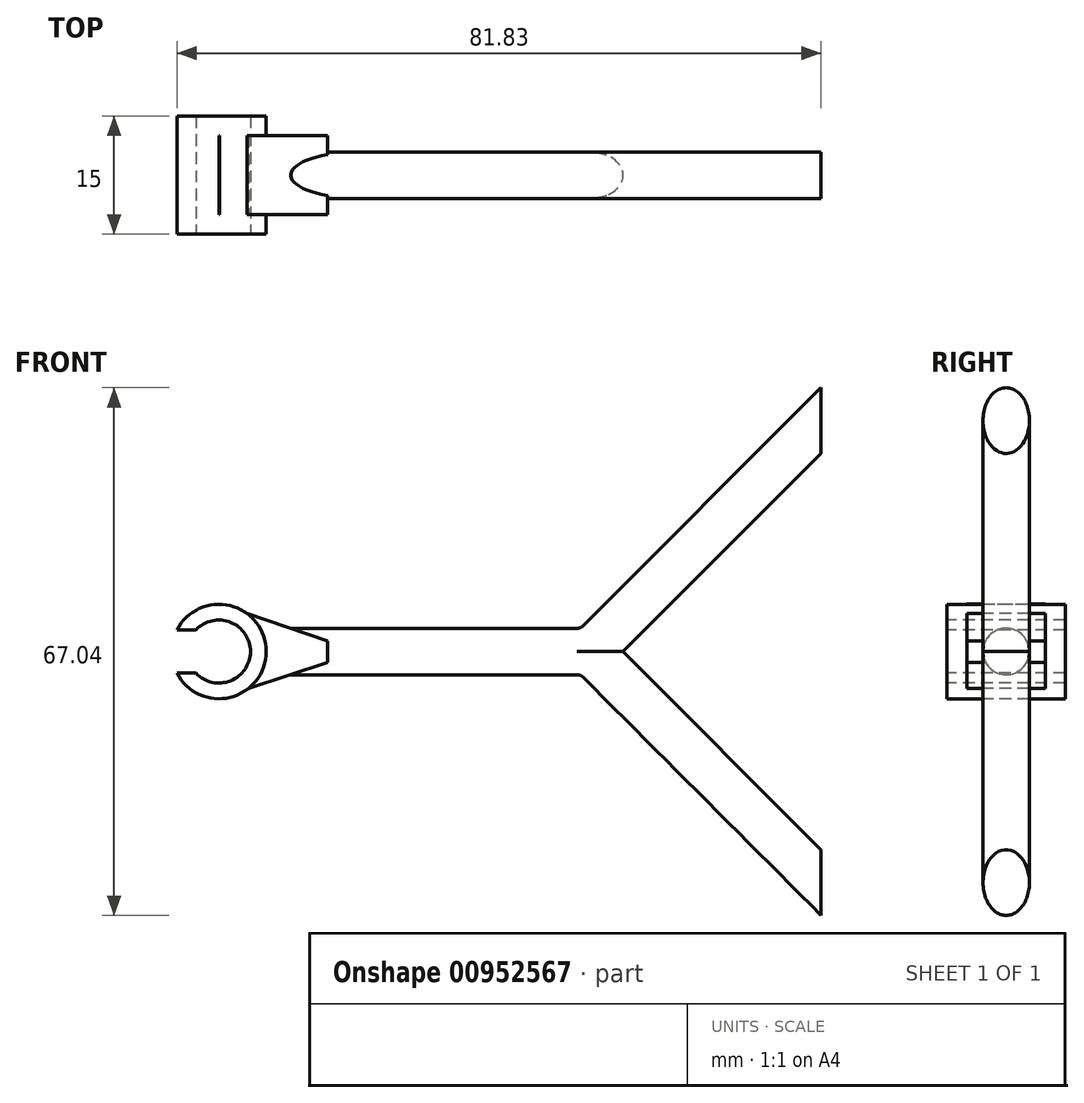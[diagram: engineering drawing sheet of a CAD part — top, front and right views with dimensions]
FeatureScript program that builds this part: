
annotation { "Feature Type Name" : "Feature", "Feature Type Description" : "" }
export const myFeature = defineFeature(function(context is Context, id is Id, definition is map)
    precondition{}
    {
        {
            var Q0;
            Q0=qCreatedBy(makeId("Front.planeOp"),FACE);
            var sketch = newSketch(context, id + "F0", { "sketchPlane" : qUnion([Q0])});
            skCircle(sketch, "E0", {"center": v(0, 0) * mm, "radius": 4 * mm});
            skCircle(sketch, "E1", {"center": v(0, 0) * mm, "radius": 6 * mm});
            skSolve(sketch);
        }
        {
            var Q0;
            Q0=qSketchRegion(id+"F0",true);
            extrude(context, id + "F1", {"entities" : qUnion([Q0]), "endBound" : BoundingType.SYMMETRIC, "oppositeDirection" : true, "depth" : 15 * mm, "offsetDistance" : 25 * mm});
        }
        {
            var Q0;
            Q0=qCreatedBy(makeId("Right.planeOp"),FACE);
            cPlane(context, id + "F2", {"entities" : qUnion([Q0]), "cplaneType" : CPlaneType.OFFSET, "offset" : 4.5 * mm, "width" : 150 * mm, "height" : 150 * mm});
        }
        {
            var Q0;
            Q0=qCreatedBy(id+"F2.planeOp",FACE);
            var sketch = newSketch(context, id + "F3", { "sketchPlane" : qUnion([Q0])});
            skCircle(sketch, "E2", {"center": v(0, 0) * mm, "radius": 2.95 * mm});
            skSolve(sketch);
        }
        {
            var Q0;
            Q0=qSketchRegion(id+"F3",true);
            extrude(context, id + "F4", {"entities" : qUnion([Q0]), "operationType" : NewBodyOperationType.ADD, "depth" : 38 * mm, "offsetDistance" : 25 * mm});
        }
        {
            var Q0;
            Q0=makeQuery(id+"F1.opExtrude","CAP_FACE",FACE,{"disambiguationData":[OSD([sQuery(id+"F0.wireOp",EDGE,"E0"),sQuery(id+"F0.wireOp",EDGE,"E1")])],"isStart":true});
            var sketch = newSketch(context, id + "F5", { "sketchPlane" : qUnion([Q0])});
            skLineSegment(sketch, "E3.bottom", {"start": v(-20, 2.75) * mm, "end": v(0, 2.75) * mm});
            skLineSegment(sketch, "E3.top", {"start": v(-20, -2.75) * mm, "end": v(0, -2.75) * mm});
            skLineSegment(sketch, "E3.left", {"start": v(-20, 2.75) * mm, "end": v(-20, -2.75) * mm});
            skLineSegment(sketch, "E3.right", {"start": v(0, 2.75) * mm, "end": v(0, -2.75) * mm});
            skPoint(sketch, "E4", {"position": v(-20, 0) * mm});
            skSolve(sketch);
        }
        {
            var Q0;
            Q0=qSketchRegion(id+"F5",true);
            extrude(context, id + "F6", {"entities" : qUnion([Q0]), "operationType" : NewBodyOperationType.REMOVE, "oppositeDirection" : true, "depth" : 25 * mm, "offsetDistance" : 25 * mm});
        }
        {
            var Q0;
            Q0=qCreatedBy(id+"F2.planeOp",FACE);
            cPlane(context, id + "F7", {"entities" : qUnion([Q0]), "cplaneType" : CPlaneType.OFFSET, "offset" : 12 * mm, "width" : 150 * mm, "height" : 150 * mm});
        }
        {
            var Q0;
            Q0=qCreatedBy(id+"F7.planeOp",FACE);
            var sketch = newSketch(context, id + "F8", { "sketchPlane" : qUnion([Q0])});
            skLineSegment(sketch, "E5", {"start": v(-2.5, 0) * mm, "end": v(2.5, 0) * mm, "construction": true});
            skPoint(sketch, "E6", {"position": v(0, 0) * mm});
            skArc(sketch, "E7", {"start": v(3.5, 0) * mm, "mid": v(2.5, 1) * mm, "end": v(1.5, 0) * mm});
            skLineSegment(sketch, "E8", {"start": v(0, 0) * mm, "end": v(0, -1.96) * mm, "construction": true});
            skArc(sketch, "E9.MirrorCS", {"start": v(-3.5, 0) * mm, "mid": v(-2.5, 1) * mm, "end": v(-1.5, 0) * mm});
            skSolve(sketch);
        }
        {
            var Q0;
            Q0=qCreatedBy(id+"F7.planeOp",FACE);
            var sketch = newSketch(context, id + "F9", { "sketchPlane" : qUnion([Q0])});
            skLineSegment(sketch, "E10", {"start": v(-4.04, 0) * mm, "end": v(4.97, 0) * mm, "construction": true});
            skSolve(sketch);
        }
        {
            var Q0;
            Q0=makeQuery(id+"F4.opExtrude","CAP_FACE",FACE,{"disambiguationData":[OSD([sQuery(id+"F3.wireOp",EDGE,"E2")])],"isStart":false});
            var sketch = newSketch(context, id + "F10", { "sketchPlane" : qUnion([Q0])});
            skCircle(sketch, "E11", {"center": v(0, 0) * mm, "radius": 2.5 * mm});
            skSolve(sketch);
        }
        {
            var Q0;
            Q0=makeQuery(id+"F0.imprint","IMPRINT",FACE,{"disambiguationData":[TD([[makeQuery(id+"F0.imprint","IMPRINT",EDGE,{"derivedFrom":sQuery(id+"F0.wireOp",EDGE,"E0")}),1.0]])]});
            var sketch = newSketch(context, id + "F11", { "sketchPlane" : qUnion([Q0])});
            skLineSegment(sketch, "E12", {"start": v(0, 6.02) * mm, "end": v(13.77, 1.37) * mm});
            skLineSegment(sketch, "E13", {"start": v(13.77, 1.37) * mm, "end": v(13.77, -1.38) * mm});
            skLineSegment(sketch, "E14", {"start": v(13.77, -1.38) * mm, "end": v(0, -5.9) * mm});
            skLineSegment(sketch, "E15", {"start": v(0, -5.9) * mm, "end": v(5.86, 0) * mm});
            skLineSegment(sketch, "E16", {"start": v(5.86, 0) * mm, "end": v(0, 6.02) * mm});
            skSolve(sketch);
        }
        {
            var Q0;
            Q0=qSketchRegion(id+"F11",true);
            extrude(context, id + "F12", {"entities" : qUnion([Q0]), "operationType" : NewBodyOperationType.ADD, "endBound" : BoundingType.SYMMETRIC, "depth" : 10 * mm, "offsetDistance" : 25 * mm});
        }
        {
            var Q0;
            Q0=qCreatedBy(makeId("Front.planeOp"),FACE);
            var sketch = newSketch(context, id + "F13", { "sketchPlane" : qUnion([Q0])});
            skLineSegment(sketch, "E17.bottom", {"start": v(37.5, 1) * mm, "end": v(34.5, 1) * mm});
            skLineSegment(sketch, "E17.top", {"start": v(37.5, -1) * mm, "end": v(34.5, -1) * mm});
            skLineSegment(sketch, "E17.left", {"start": v(37.5, 1) * mm, "end": v(37.5, -1) * mm});
            skLineSegment(sketch, "E17.right", {"start": v(34.5, 1) * mm, "end": v(34.5, -1) * mm});
            skPoint(sketch, "E18", {"position": v(37.5, 0) * mm});
            skPoint(sketch, "E19", {"position": v(42.5, 0) * mm});
            skSolve(sketch);
        }
        {
            var Q0;
            Q0=makeQuery(id+"F10.imprint","IMPRINT",FACE,{"disambiguationData":[TD([[makeQuery(id+"F10.imprint","IMPRINT",EDGE,{"derivedFrom":sQuery(id+"F10.wireOp",EDGE,"E11")}),1.0]])]});
            var sketch = newSketch(context, id + "F14", { "sketchPlane" : qUnion([Q0])});
            skCircle(sketch, "E20", {"center": v(0, 0) * mm, "radius": 2.95 * mm});
            skSolve(sketch);
        }
        {
            var Q0;
            Q0=qCreatedBy(makeId("Front.planeOp"),FACE);
            var sketch = newSketch(context, id + "F15", { "sketchPlane" : qUnion([Q0])});
            skLineSegment(sketch, "E21", {"start": v(42.5, 0) * mm, "end": v(45.5, 0) * mm});
            skLineSegment(sketch, "E22", {"start": v(49.5, -4) * mm, "end": v(49.5, -8.25) * mm, "construction": true});
            skPoint(sketch, "E23.visualSharp", {"position": v(49.5, 0) * mm});
            skArc(sketch, "E23.filletArc", {"start": v(49.5, -4) * mm, "mid": v(49.2, -2.47) * mm, "end": v(48.33, -1.17) * mm, "construction": true});
            skArc(sketch, "E24", {"start": v(48.33, -1.17) * mm, "mid": v(47.03, -0.3) * mm, "end": v(45.5, 0) * mm});
            skLineSegment(sketch, "E25", {"start": v(49.5, 0) * mm, "end": v(45.5, -4) * mm, "construction": true});
            skLineSegment(sketch, "E26", {"start": v(48.33, -1.17) * mm, "end": v(83.68, -36.53) * mm});
            skArc(sketch, "E27.MirrorCS", {"start": v(48.33, 1.17) * mm, "mid": v(47.03, 0.3) * mm, "end": v(45.5, 0) * mm});
            skLineSegment(sketch, "E28.MirrorCS", {"start": v(48.33, 1.17) * mm, "end": v(83.68, 36.53) * mm});
            skLineSegment(sketch, "E29.MirrorCS", {"start": v(49.5, 0) * mm, "end": v(45.5, 4) * mm, "construction": true});
            skLineSegment(sketch, "E30.MirrorCS", {"start": v(49.5, 4) * mm, "end": v(49.5, 8.25) * mm, "construction": true});
            skArc(sketch, "E31.MirrorCS", {"start": v(49.5, 4) * mm, "mid": v(49.2, 2.47) * mm, "end": v(48.33, 1.17) * mm, "construction": true});
            skSolve(sketch);
        }
        {
            var Q0;
            Q0=qSketchRegion(id+"F14",true);
            var Q1;
            Q1=sQuery(id+"F15.wireOp",EDGE,"E21");
            var Q2;
            Q2=sQuery(id+"F15.wireOp",EDGE,"E27.MirrorCS");
            var Q3;
            Q3=sQuery(id+"F15.wireOp",EDGE,"E28.MirrorCS");
            sweep(context, id + "F16", {"operationType" : NewBodyOperationType.ADD, "profiles" : qUnion([Q0]), "surfaceOperationType" : NewSurfaceOperationType.ADD, "path" : qUnion([Q1, Q2, Q3])});
        }
        {
            var Q0;
            Q0=qSketchRegion(id+"F14",true);
            var Q1;
            Q1=sQuery(id+"F15.wireOp",EDGE,"E21");
            var Q2;
            Q2=sQuery(id+"F15.wireOp",EDGE,"E24");
            var Q3;
            Q3=sQuery(id+"F15.wireOp",EDGE,"E26");
            sweep(context, id + "F17", {"operationType" : NewBodyOperationType.ADD, "profiles" : qUnion([Q0]), "path" : qUnion([Q1, Q2, Q3])});
        }
        {
            var Q0;
            Q0=qCreatedBy(id+"F7.planeOp",FACE);
            cPlane(context, id + "F18", {"entities" : qUnion([Q0]), "cplaneType" : CPlaneType.OFFSET, "offset" : 70 * mm, "width" : 150 * mm, "height" : 150 * mm});
        }
        {
            var Q0;
            Q0=qCreatedBy(id+"F18.planeOp",FACE);
            var sketch = newSketch(context, id + "F19", { "sketchPlane" : qUnion([Q0])});
            skLineSegment(sketch, "E32.bottom", {"start": v(-12.72, 45.9) * mm, "end": v(13.64, 45.9) * mm});
            skLineSegment(sketch, "E32.top", {"start": v(-12.72, -45.9) * mm, "end": v(13.64, -45.9) * mm});
            skLineSegment(sketch, "E32.left", {"start": v(-12.72, 45.9) * mm, "end": v(-12.72, -45.9) * mm});
            skLineSegment(sketch, "E32.right", {"start": v(13.64, 45.9) * mm, "end": v(13.64, -45.9) * mm});
            skPoint(sketch, "E33", {"position": v(0.46, 45.9) * mm});
            skPoint(sketch, "E34.positionSnap0", {"position": v(13.64, 0) * mm});
            skSolve(sketch);
        }
        {
            var Q0;
            Q0 = qSketchRegion(id + "F19", true);
            extrude(context, id + "F20", {"entities" : qUnion([Q0]), "operationType" : NewBodyOperationType.REMOVE, "oppositeDirection" : true, "depth" : 10 * mm, "offsetDistance" : 25 * mm});
        }
    });
